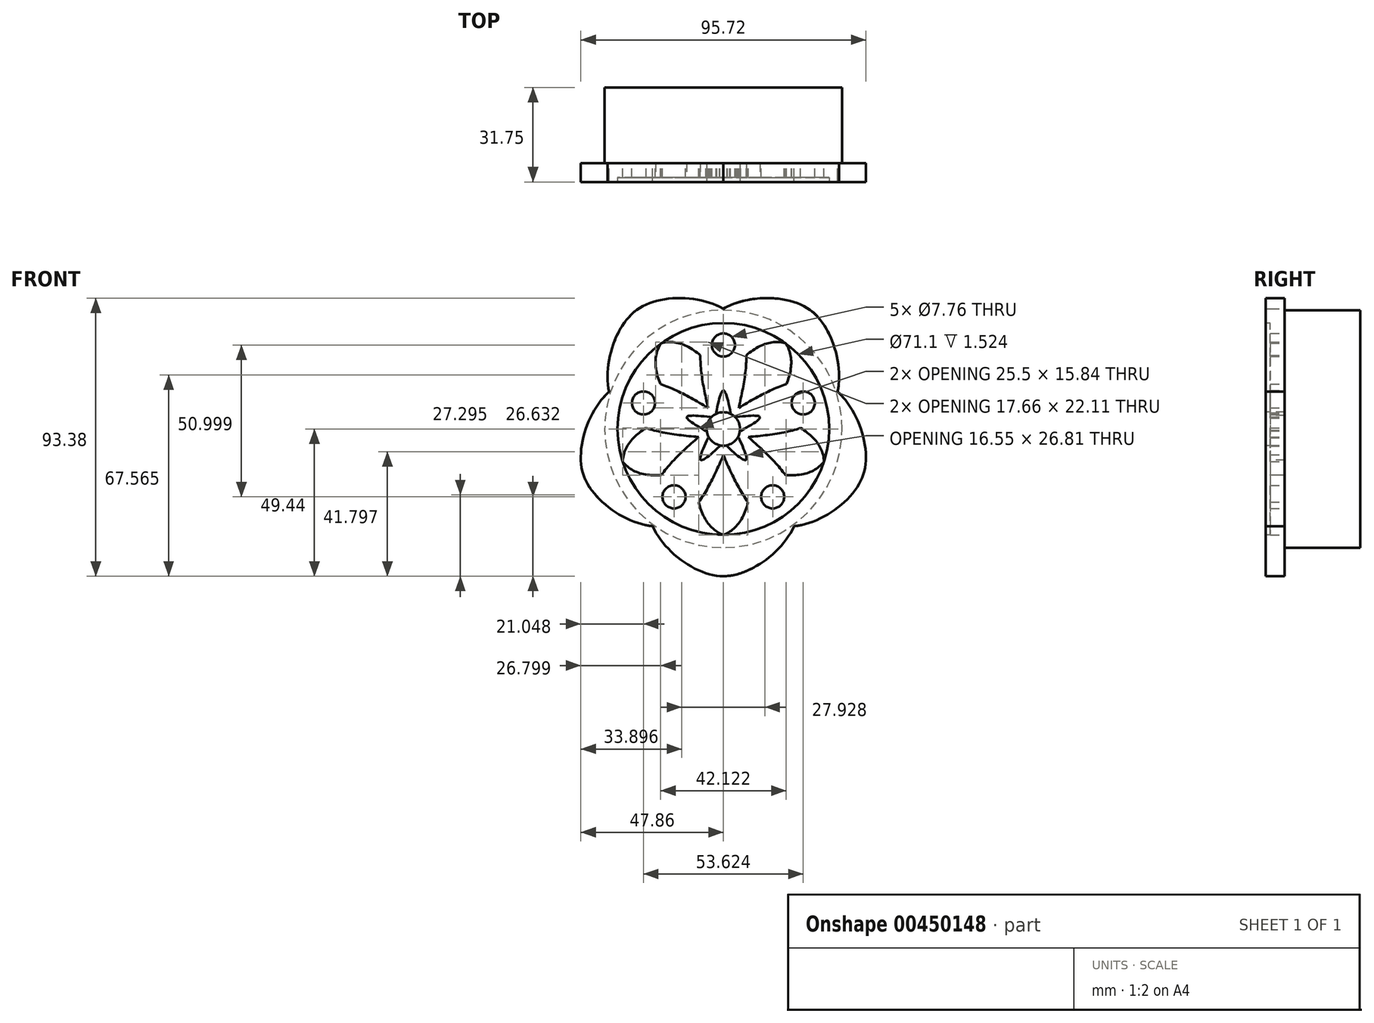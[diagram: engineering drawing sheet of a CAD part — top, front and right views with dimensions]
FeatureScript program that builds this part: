
annotation { "Feature Type Name" : "Feature", "Feature Type Description" : "" }
export const myFeature = defineFeature(function(context is Context, id is Id, definition is map)
    precondition{}
    {
        {
            var Q0;
            Q0=qCreatedBy(makeId("Front.planeOp"),FACE);
            var sketch = newSketch(context, id + "F0", { "sketchPlane" : qUnion([Q0])});
            skArc(sketch, "E0", {"start": v(0, 39.56) * mm, "mid": v(-23.25, -32) * mm, "end": v(37.62, 12.22) * mm});
            skCircle(sketch, "E1", {"center": v(0, 0) * mm, "radius": 3.4 * mm});
            skLineSegment(sketch, "E2", {"start": v(0, 0) * mm, "end": v(37.62, 12.22) * mm});
            skLineSegment(sketch, "E3", {"start": v(0, 0) * mm, "end": v(0, 39.56) * mm});
            skLineSegment(sketch, "E4", {"start": v(-3.4, 0) * mm, "end": v(-3.4, -16.87) * mm});
            skFitSpline(sketch, "E5", {"points": [v(-3.4, 0) * mm, v(37.62, 12.22) * mm], "startDerivative": vector(0, 113.2) * mm, "endDerivative": vector(27.48, -84.58) * mm});
            skFitSpline(sketch, "E6.MirrorCS", {"points": [v(3.4, 0) * mm, v(-37.62, 12.22) * mm], "startDerivative": vector(0, 113.2) * mm, "endDerivative": vector(-27.48, -84.58) * mm});
            skSolve(sketch);
        }
        {
            var Q0;
            Q0=qCreatedBy(makeId("Front.planeOp"),FACE);
            var sketch = newSketch(context, id + "F1", { "sketchPlane" : qUnion([Q0])});
            skCircle(sketch, "E7.0", {"center": v(0, 0) * mm, "radius": 3.4 * mm, "construction": true});
            skFitSpline(sketch, "E8", {"points": [v(-3.4, 0) * mm, v(0, 12.9) * mm, v(3.4, 0) * mm], "startDerivative": vector(6.79, 38.67) * mm, "endDerivative": vector(6.79, -38.67) * mm});
            skFitSpline(sketch, "E9", {"points": [v(-37.62, 12.22) * mm, v(-31.81, 21.17) * mm, v(-21.7, 28.51) * mm, v(-12.98, 28.11) * mm, v(-4.45, 20.78) * mm, v(-2.86, 11.66) * mm, v(-3.4, 0) * mm], "startDerivative": vector(29.93, 53.92) * mm, "endDerivative": vector(2.05, -64.5) * mm});
            skLineSegment(sketch, "E10.0", {"start": v(0, 0) * mm, "end": v(0, 39.56) * mm, "construction": true});
            skFitSpline(sketch, "E11.MirrorCS", {"points": [v(37.62, 12.22) * mm, v(31.81, 21.17) * mm, v(21.7, 28.51) * mm, v(12.98, 28.11) * mm, v(4.45, 20.78) * mm, v(2.86, 11.66) * mm, v(3.4, 0) * mm], "startDerivative": vector(-29.93, 53.92) * mm, "endDerivative": vector(-2.05, -64.5) * mm});
            skFitSpline(sketch, "E12.0", {"points": [v(3.4, 0) * mm, v(3.4, 37.73) * mm, v(-28.46, 40.42) * mm, v(-37.62, 12.22) * mm]});
            skFitSpline(sketch, "E13.0", {"points": [v(-3.4, 0) * mm, v(-3.4, 37.73) * mm, v(28.46, 40.42) * mm, v(37.62, 12.22) * mm]});
            skPoint(sketch, "E14.visualSharp", {"position": v(0, 18.48) * mm});
            skArc(sketch, "E14.filletArc", {"start": v(-3.05, 23.74) * mm, "mid": v(0, 22.22) * mm, "end": v(3.05, 23.74) * mm});
            skCircle(sketch, "E15", {"center": v(0, 28.2) * mm, "radius": 3.88 * mm});
            skSolve(sketch);
        }
        {
            var Q0;
            Q0 = qSketchRegion(id + "F1", true);
            extrude(context, id + "F2", {"entities" : qUnion([Q0]), "depth" : 4.83 * mm});
        }
        {
            var Q0;
            Q0=qCreatedBy(makeId("Right.planeOp"),FACE);
            var sketch = newSketch(context, id + "F3", { "sketchPlane" : qUnion([Q0])});
            skLineSegment(sketch, "E16", {"start": v(0, 0) * mm, "end": v(-26.1, 0) * mm});
            skSolve(sketch);
        }
        {
            var Q0;
            Q0=makeQuery(id+"F2.opExtrude","SWEPT_BODY",BODY,{"disambiguationData":[OSD([sQuery(id+"F1.wireOp",EDGE,"E8"),sQuery(id+"F1.wireOp",EDGE,"E9"),sQuery(id+"F1.wireOp",EDGE,"E11.MirrorCS"),sQuery(id+"F1.wireOp",EDGE,"E12.0"),sQuery(id+"F1.wireOp",EDGE,"E13.0"),sQuery(id+"F1.wireOp",EDGE,"E14.filletArc")])]});
            var Q1;
            Q1=makeQuery(id+"F2.opExtrude","SWEPT_BODY",BODY,{"disambiguationData":[OSD([sQuery(id+"F1.wireOp",EDGE,"E15")])]});
            var Q2;
            Q2=sQuery(id+"F3.wireOp",EDGE,"E16");
            circularPattern(context, id + "F4", {"entities" : qUnion([Q0, Q1]), "axis" : qUnion([Q2]), "angle" : 360 * degree, "instanceCount" : 5, "equalSpace" : true});
        }
        {
            var Q0;
            Q0=qCreatedBy(makeId("Front.planeOp"),FACE);
            var sketch = newSketch(context, id + "F5", { "sketchPlane" : qUnion([Q0])});
            skArc(sketch, "E17.0.0", {"start": v(-16.42, -17.41) * mm, "mid": v(-13.06, -17.97) * mm, "end": v(-11.49, -21) * mm});
            skFitSpline(sketch, "E17.0.1", {"points": [v(-2.75, 2) * mm, v(-24.92, -28.53) * mm, v(-0.73, -49.43) * mm, v(23.25, -32) * mm]});
            skFitSpline(sketch, "E17.0.2", {"points": [v(23.25, -32) * mm, v(20.14, -33.45) * mm, v(13.7, -36.62) * mm, v(0.38, -37.05) * mm, v(-6.87, -31.08) * mm, v(-10.06, -19) * mm, v(-4.75, -10.91) * mm, v(0.64, -5.1) * mm, v(2.75, -2) * mm]});
            skFitSpline(sketch, "E17.0.3", {"points": [v(2.75, -2) * mm, v(-1.96, -6.54) * mm, v(-11.37, -15.64) * mm, v(-5.62, -3.88) * mm, v(-2.75, 2) * mm]});
            skFitSpline(sketch, "E17.0.4", {"points": [v(-2.75, 2) * mm, v(-5.05, -0.97) * mm, v(-8.9, -7.9) * mm, v(-14.97, -15.44) * mm, v(-27.43, -16.13) * mm, v(-35.35, -11.09) * mm, v(-39.05, 1.7) * mm, v(-38.04, 8.82) * mm, v(-37.62, 12.22) * mm]});
            skFitSpline(sketch, "E17.0.5", {"points": [v(-37.62, 12.22) * mm, v(-46.78, -15.97) * mm, v(-19.43, -32.52) * mm, v(2.75, -2) * mm]});
            skArc(sketch, "E17.1.0", {"start": v(-21.64, 10.23) * mm, "mid": v(-21.13, 6.87) * mm, "end": v(-23.52, 4.44) * mm});
            skFitSpline(sketch, "E17.1.1", {"points": [v(1.05, 3.23) * mm, v(-34.84, 14.89) * mm, v(-47.24, -14.58) * mm, v(-23.25, -32) * mm]});
            skFitSpline(sketch, "E17.1.2", {"points": [v(-23.25, -32) * mm, v(-25.59, -29.5) * mm, v(-30.6, -24.34) * mm, v(-35.12, -11.81) * mm, v(-31.68, -3.07) * mm, v(-21.18, 3.7) * mm, v(-11.85, 1.15) * mm, v(-4.66, -2.18) * mm, v(-1.05, -3.23) * mm]});
            skFitSpline(sketch, "E17.1.3", {"points": [v(-1.05, -3.23) * mm, v(-6.83, -0.16) * mm, v(-18.4, 5.98) * mm, v(-5.43, 4.14) * mm, v(1.05, 3.23) * mm]});
            skFitSpline(sketch, "E17.1.4", {"points": [v(1.05, 3.23) * mm, v(-2.48, 4.5) * mm, v(-10.26, 6.03) * mm, v(-19.3, 9.47) * mm, v(-23.82, 21.1) * mm, v(-21.47, 30.2) * mm, v(-10.45, 37.67) * mm, v(-3.37, 38.9) * mm, v(0, 39.56) * mm]});
            skFitSpline(sketch, "E17.1.5", {"points": [v(0, 39.56) * mm, v(-29.65, 39.56) * mm, v(-36.93, 8.43) * mm, v(-1.05, -3.23) * mm]});
            skArc(sketch, "E17.2.0", {"start": v(3.05, 23.74) * mm, "mid": v(0, 22.22) * mm, "end": v(-3.05, 23.74) * mm});
            skFitSpline(sketch, "E17.2.1", {"points": [v(3.4, 0) * mm, v(3.4, 37.73) * mm, v(-28.46, 40.42) * mm, v(-37.62, 12.22) * mm]});
            skFitSpline(sketch, "E17.2.2", {"points": [v(-37.62, 12.22) * mm, v(-35.96, 15.22) * mm, v(-32.6, 21.57) * mm, v(-22.08, 29.75) * mm, v(-12.71, 29.18) * mm, v(-3.04, 21.29) * mm, v(-2.57, 11.62) * mm, v(-3.51, 3.75) * mm, v(-3.4, 0) * mm]});
            skFitSpline(sketch, "E17.2.3", {"points": [v(-3.4, 0) * mm, v(-2.26, 6.45) * mm, v(0, 19.34) * mm, v(2.26, 6.45) * mm, v(3.4, 0) * mm]});
            skFitSpline(sketch, "E17.2.4", {"points": [v(3.4, 0) * mm, v(3.51, 3.75) * mm, v(2.57, 11.62) * mm, v(3.04, 21.29) * mm, v(12.71, 29.18) * mm, v(22.08, 29.75) * mm, v(32.6, 21.57) * mm, v(35.96, 15.22) * mm, v(37.62, 12.22) * mm]});
            skFitSpline(sketch, "E17.2.5", {"points": [v(37.62, 12.22) * mm, v(28.46, 40.42) * mm, v(-3.4, 37.73) * mm, v(-3.4, 0) * mm]});
            skArc(sketch, "E17.3.0", {"start": v(23.52, 4.44) * mm, "mid": v(21.13, 6.87) * mm, "end": v(21.64, 10.23) * mm});
            skFitSpline(sketch, "E17.3.1", {"points": [v(1.05, -3.23) * mm, v(36.93, 8.43) * mm, v(29.65, 39.56) * mm, v(0, 39.56) * mm]});
            skFitSpline(sketch, "E17.3.2", {"points": [v(0, 39.56) * mm, v(3.37, 38.9) * mm, v(10.45, 37.67) * mm, v(21.47, 30.2) * mm, v(23.82, 21.1) * mm, v(19.3, 9.47) * mm, v(10.26, 6.03) * mm, v(2.48, 4.5) * mm, v(-1.05, 3.23) * mm]});
            skFitSpline(sketch, "E17.3.3", {"points": [v(-1.05, 3.23) * mm, v(5.43, 4.14) * mm, v(18.4, 5.98) * mm, v(6.83, -0.16) * mm, v(1.05, -3.23) * mm]});
            skFitSpline(sketch, "E17.3.4", {"points": [v(1.05, -3.23) * mm, v(4.66, -2.18) * mm, v(11.85, 1.15) * mm, v(21.18, 3.7) * mm, v(31.68, -3.07) * mm, v(35.12, -11.81) * mm, v(30.6, -24.34) * mm, v(25.59, -29.5) * mm, v(23.25, -32) * mm]});
            skFitSpline(sketch, "E17.3.5", {"points": [v(23.25, -32) * mm, v(47.24, -14.58) * mm, v(34.84, 14.89) * mm, v(-1.05, 3.23) * mm]});
            skArc(sketch, "E17.4.0", {"start": v(11.49, -21) * mm, "mid": v(13.06, -17.97) * mm, "end": v(16.42, -17.41) * mm});
            skFitSpline(sketch, "E17.4.1", {"points": [v(-2.75, -2) * mm, v(19.43, -32.52) * mm, v(46.78, -15.97) * mm, v(37.62, 12.22) * mm]});
            skFitSpline(sketch, "E17.4.2", {"points": [v(37.62, 12.22) * mm, v(38.04, 8.82) * mm, v(39.05, 1.7) * mm, v(35.35, -11.09) * mm, v(27.43, -16.13) * mm, v(14.97, -15.44) * mm, v(8.9, -7.9) * mm, v(5.05, -0.97) * mm, v(2.75, 2) * mm]});
            skFitSpline(sketch, "E17.4.3", {"points": [v(2.75, 2) * mm, v(5.62, -3.88) * mm, v(11.37, -15.64) * mm, v(1.96, -6.54) * mm, v(-2.75, -2) * mm]});
            skFitSpline(sketch, "E17.4.4", {"points": [v(-2.75, -2) * mm, v(-0.64, -5.1) * mm, v(4.75, -10.91) * mm, v(10.06, -19) * mm, v(6.87, -31.08) * mm, v(-0.38, -37.05) * mm, v(-13.7, -36.62) * mm, v(-20.14, -33.45) * mm, v(-23.25, -32) * mm]});
            skFitSpline(sketch, "E17.4.5", {"points": [v(-23.25, -32) * mm, v(0.73, -49.43) * mm, v(24.92, -28.53) * mm, v(2.75, 2) * mm]});
            skCircle(sketch, "E17.5", {"center": v(16.57, -22.8) * mm, "radius": 3.88 * mm});
            skCircle(sketch, "E17.6.0", {"center": v(26.81, 8.71) * mm, "radius": 3.88 * mm});
            skCircle(sketch, "E17.7.0", {"center": v(0, 28.2) * mm, "radius": 3.88 * mm});
            skCircle(sketch, "E17.8.0", {"center": v(-26.81, 8.71) * mm, "radius": 3.88 * mm});
            skCircle(sketch, "E17.9.0", {"center": v(-16.57, -22.8) * mm, "radius": 3.88 * mm});
            skPoint(sketch, "E18.orphan", {"position": v(-37.62, 12.22) * mm});
            skPoint(sketch, "E19.orphan", {"position": v(0, 39.56) * mm});
            skPoint(sketch, "E20.orphan", {"position": v(37.62, 12.22) * mm});
            skPoint(sketch, "E21.orphan", {"position": v(23.25, -32) * mm});
            skPoint(sketch, "E22.orphan", {"position": v(-23.25, -32) * mm});
            skFitSpline(sketch, "E23.trimOffspring", {"points": [v(-2.75, 2) * mm, v(-5.05, -0.97) * mm, v(-8.9, -7.9) * mm, v(-14.97, -15.44) * mm, v(-27.43, -16.13) * mm, v(-35.35, -11.09) * mm, v(-39.05, 1.7) * mm, v(-38.04, 8.82) * mm, v(-37.62, 12.22) * mm]});
            skFitSpline(sketch, "E24.trimOffspring", {"points": [v(-37.62, 12.22) * mm, v(-35.96, 15.22) * mm, v(-32.6, 21.57) * mm, v(-22.08, 29.75) * mm, v(-12.71, 29.18) * mm, v(-3.04, 21.29) * mm, v(-2.57, 11.62) * mm, v(-3.51, 3.75) * mm, v(-3.4, 0) * mm]});
            skFitSpline(sketch, "E25.trimOffspring", {"points": [v(1.05, 3.23) * mm, v(-2.48, 4.5) * mm, v(-10.26, 6.03) * mm, v(-19.3, 9.47) * mm, v(-23.82, 21.1) * mm, v(-21.47, 30.2) * mm, v(-10.45, 37.67) * mm, v(-3.37, 38.9) * mm, v(0, 39.56) * mm]});
            skFitSpline(sketch, "E26.trimOffspring", {"points": [v(-1.05, -3.23) * mm, v(-6.83, -0.16) * mm, v(-18.4, 5.98) * mm, v(-5.43, 4.14) * mm, v(1.05, 3.23) * mm]});
            skFitSpline(sketch, "E27.trimOffspring", {"points": [v(-3.4, 0) * mm, v(-2.26, 6.45) * mm, v(0, 19.34) * mm, v(2.26, 6.45) * mm, v(3.4, 0) * mm]});
            skFitSpline(sketch, "E28.trimOffspring", {"points": [v(2.75, -2) * mm, v(-1.96, -6.54) * mm, v(-11.37, -15.64) * mm, v(-5.62, -3.88) * mm, v(-2.75, 2) * mm]});
            skFitSpline(sketch, "E29.trimOffspring", {"points": [v(-1.05, -3.23) * mm, v(-6.83, -0.16) * mm, v(-18.4, 5.98) * mm, v(-5.43, 4.14) * mm, v(1.05, 3.23) * mm]});
            skFitSpline(sketch, "E30.trimOffspring", {"points": [v(-23.25, -32) * mm, v(-25.59, -29.5) * mm, v(-30.6, -24.34) * mm, v(-35.12, -11.81) * mm, v(-31.68, -3.07) * mm, v(-21.18, 3.7) * mm, v(-11.85, 1.15) * mm, v(-4.66, -2.18) * mm, v(-1.05, -3.23) * mm]});
            skFitSpline(sketch, "E31.trimOffspring", {"points": [v(-2.75, -2) * mm, v(-0.64, -5.1) * mm, v(4.75, -10.91) * mm, v(10.06, -19) * mm, v(6.87, -31.08) * mm, v(-0.38, -37.05) * mm, v(-13.7, -36.62) * mm, v(-20.14, -33.45) * mm, v(-23.25, -32) * mm]});
            skFitSpline(sketch, "E32.trimOffspring", {"points": [v(2.75, 2) * mm, v(5.62, -3.88) * mm, v(11.37, -15.64) * mm, v(1.96, -6.54) * mm, v(-2.75, -2) * mm]});
            skFitSpline(sketch, "E33.trimOffspring", {"points": [v(2.75, -2) * mm, v(-1.96, -6.54) * mm, v(-11.37, -15.64) * mm, v(-5.62, -3.88) * mm, v(-2.75, 2) * mm]});
            skFitSpline(sketch, "E34.trimOffspring", {"points": [v(23.25, -32) * mm, v(20.14, -33.45) * mm, v(13.7, -36.62) * mm, v(0.38, -37.05) * mm, v(-6.87, -31.08) * mm, v(-10.06, -19) * mm, v(-4.75, -10.91) * mm, v(0.64, -5.1) * mm, v(2.75, -2) * mm]});
            skFitSpline(sketch, "E35.trimOffspring", {"points": [v(1.05, -3.23) * mm, v(4.66, -2.18) * mm, v(11.85, 1.15) * mm, v(21.18, 3.7) * mm, v(31.68, -3.07) * mm, v(35.12, -11.81) * mm, v(30.6, -24.34) * mm, v(25.59, -29.5) * mm, v(23.25, -32) * mm]});
            skFitSpline(sketch, "E36.trimOffspring", {"points": [v(-1.05, 3.23) * mm, v(5.43, 4.14) * mm, v(18.4, 5.98) * mm, v(6.83, -0.16) * mm, v(1.05, -3.23) * mm]});
            skFitSpline(sketch, "E37.trimOffspring", {"points": [v(2.75, 2) * mm, v(5.62, -3.88) * mm, v(11.37, -15.64) * mm, v(1.96, -6.54) * mm, v(-2.75, -2) * mm]});
            skFitSpline(sketch, "E38.trimOffspring", {"points": [v(37.62, 12.22) * mm, v(38.04, 8.82) * mm, v(39.05, 1.7) * mm, v(35.35, -11.09) * mm, v(27.43, -16.13) * mm, v(14.97, -15.44) * mm, v(8.9, -7.9) * mm, v(5.05, -0.97) * mm, v(2.75, 2) * mm]});
            skFitSpline(sketch, "E39.trimOffspring", {"points": [v(3.4, 0) * mm, v(3.51, 3.75) * mm, v(2.57, 11.62) * mm, v(3.04, 21.29) * mm, v(12.71, 29.18) * mm, v(22.08, 29.75) * mm, v(32.6, 21.57) * mm, v(35.96, 15.22) * mm, v(37.62, 12.22) * mm]});
            skFitSpline(sketch, "E40.trimOffspring", {"points": [v(-3.4, 0) * mm, v(-2.26, 6.45) * mm, v(0, 19.34) * mm, v(2.26, 6.45) * mm, v(3.4, 0) * mm]});
            skFitSpline(sketch, "E41.trimOffspring", {"points": [v(-1.05, 3.23) * mm, v(5.43, 4.14) * mm, v(18.4, 5.98) * mm, v(6.83, -0.16) * mm, v(1.05, -3.23) * mm]});
            skFitSpline(sketch, "E42.trimOffspring", {"points": [v(0, 39.56) * mm, v(3.37, 38.9) * mm, v(10.45, 37.67) * mm, v(21.47, 30.2) * mm, v(23.82, 21.1) * mm, v(19.3, 9.47) * mm, v(10.26, 6.03) * mm, v(2.48, 4.5) * mm, v(-1.05, 3.23) * mm]});
            skSolve(sketch);
        }
        {
            var Q0;
            Q0 = qSketchRegion(id + "F5", true);
            extrude(context, id + "F6", {"entities" : qUnion([Q0]), "depth" : 6.35 * mm});
        }
        {
            var Q0;
            Q0=makeQuery(id+"F6.opExtrude","CAP_FACE",FACE,{"disambiguationData":[OSD([sQuery(id+"F5.wireOp",EDGE,"E17.0.0"),sQuery(id+"F5.wireOp",EDGE,"E17.0.1"),sQuery(id+"F5.wireOp",EDGE,"E17.0.2"),sQuery(id+"F5.wireOp",EDGE,"E17.0.5"),sQuery(id+"F5.wireOp",EDGE,"E17.1.0"),sQuery(id+"F5.wireOp",EDGE,"E17.1.1"),sQuery(id+"F5.wireOp",EDGE,"E17.1.2"),sQuery(id+"F5.wireOp",EDGE,"E17.1.5"),sQuery(id+"F5.wireOp",EDGE,"E17.2.0"),sQuery(id+"F5.wireOp",EDGE,"E17.2.1"),sQuery(id+"F5.wireOp",EDGE,"E17.2.2"),sQuery(id+"F5.wireOp",EDGE,"E17.2.5"),sQuery(id+"F5.wireOp",EDGE,"E17.3.0"),sQuery(id+"F5.wireOp",EDGE,"E17.3.1"),sQuery(id+"F5.wireOp",EDGE,"E17.3.2"),sQuery(id+"F5.wireOp",EDGE,"E17.3.5"),sQuery(id+"F5.wireOp",EDGE,"E17.4.0"),sQuery(id+"F5.wireOp",EDGE,"E17.4.1"),sQuery(id+"F5.wireOp",EDGE,"E17.4.2"),sQuery(id+"F5.wireOp",EDGE,"E17.4.5"),sQuery(id+"F5.wireOp",EDGE,"E23.trimOffspring"),sQuery(id+"F5.wireOp",EDGE,"E25.trimOffspring"),sQuery(id+"F5.wireOp",EDGE,"E27.trimOffspring"),sQuery(id+"F5.wireOp",EDGE,"E29.trimOffspring"),sQuery(id+"F5.wireOp",EDGE,"E31.trimOffspring"),sQuery(id+"F5.wireOp",EDGE,"E33.trimOffspring"),sQuery(id+"F5.wireOp",EDGE,"E35.trimOffspring"),sQuery(id+"F5.wireOp",EDGE,"E37.trimOffspring"),sQuery(id+"F5.wireOp",EDGE,"E39.trimOffspring"),sQuery(id+"F5.wireOp",EDGE,"E41.trimOffspring")])],"isStart":false});
            var sketch = newSketch(context, id + "F7", { "sketchPlane" : qUnion([Q0])});
            skCircle(sketch, "E43", {"center": v(0, 0) * mm, "radius": 5.63 * mm});
            skCircle(sketch, "E44", {"center": v(0, 0) * mm, "radius": 35.55 * mm});
            skCircle(sketch, "E45", {"center": v(0, 0) * mm, "radius": 39.87 * mm});
            skSolve(sketch);
        }
        {
            var Q0;
            Q0 = qSketchRegion(id + "F7", true);
            var Q1;
            {var subQ3=sQuery(id+"F7.wireOp",EDGE,"E43");var subQ7=makeQuery(id+"F6.opExtrude","CAP_EDGE",EDGE,{"disambiguationData":[OSD([sQuery(id+"F5.wireOp",EDGE,"E27.trimOffspring")])],"isStart":false});var subQ9=makeQuery(id+"F7.imprint","INTERSECT",VERTEX,{"disambiguationData":[OD(0.0)],"derivedFrom":[subQ7,subQ3]});Q1=makeQuery(id+"F7.imprint","IMPRINT",FACE,{"disambiguationData":[TD([[makeQuery(id+"F7.imprint","IMPRINT",EDGE,{"disambiguationData":[TD([[subQ9,-1.0]])],"derivedFrom":subQ3}),1.0]])]});}
            extrude(context, id + "F8", {"entities" : qUnion([Q0, Q1]), "operationType" : NewBodyOperationType.ADD, "oppositeDirection" : true, "depth" : 6.35 * mm});
        }
        {
            var Q0;
            Q0=qCreatedBy(makeId("Front.planeOp"),FACE);
            var sketch = newSketch(context, id + "F9", { "sketchPlane" : qUnion([Q0])});
            skCircle(sketch, "E46.0.0", {"center": v(0, 0) * mm, "radius": 39.87 * mm});
            skSolve(sketch);
        }
        {
            var Q0;
            Q0=qCreatedBy(makeId("Front.planeOp"),FACE);
            var sketch = newSketch(context, id + "F10", { "sketchPlane" : qUnion([Q0])});
            skCircle(sketch, "E47.0", {"center": v(0, 0) * mm, "radius": 39.87 * mm});
            skSolve(sketch);
        }
        {
            var Q0;
            Q0 = qSketchRegion(id + "F10", true);
            extrude(context, id + "F11", {"entities" : qUnion([Q0]), "oppositeDirection" : true, "depth" : 25.4 * mm});
        }
    });
